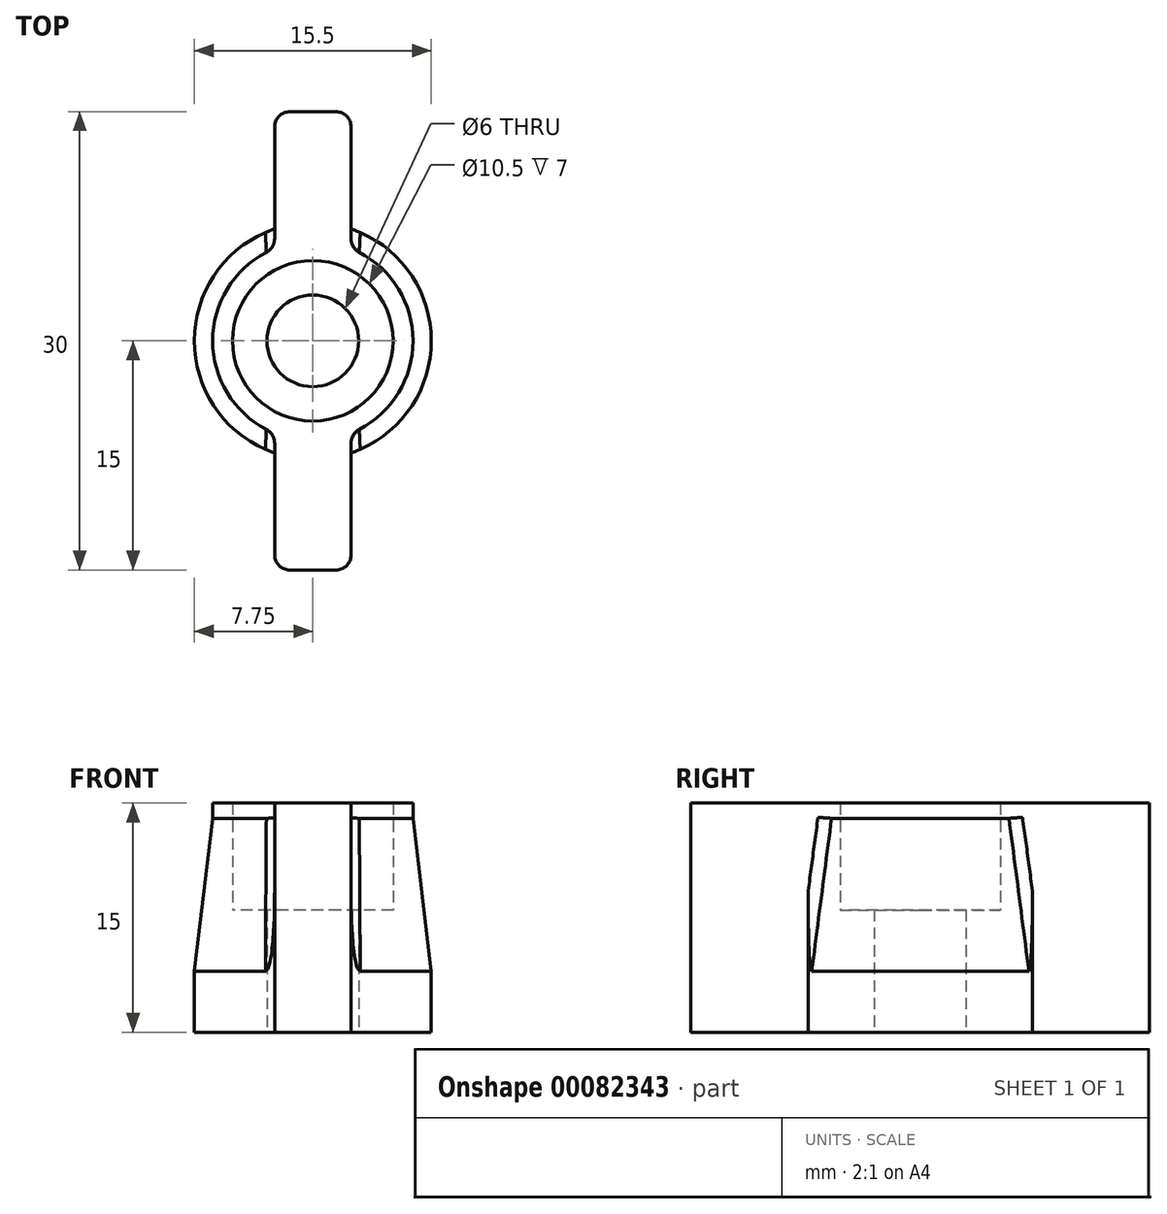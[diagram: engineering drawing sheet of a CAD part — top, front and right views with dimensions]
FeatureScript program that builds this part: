
annotation { "Feature Type Name" : "Feature", "Feature Type Description" : "" }
export const myFeature = defineFeature(function(context is Context, id is Id, definition is map)
    precondition{}
    {
        {
            var Q0;
            Q0=qCreatedBy(makeId("Top.planeOp"),FACE);
            var sketch = newSketch(context, id + "F0", { "sketchPlane" : qUnion([Q0])});
            skCircle(sketch, "E0", {"center": v(0, 0) * mm, "radius": 7.75 * mm});
            skCircle(sketch, "E1", {"center": v(0, 0) * mm, "radius": 5.25 * mm});
            skCircle(sketch, "E2", {"center": v(0, 0) * mm, "radius": 3 * mm});
            skLineSegment(sketch, "E3", {"start": v(0, 15) * mm, "end": v(-2.5, 15) * mm});
            skLineSegment(sketch, "E4", {"start": v(-2.5, 15) * mm, "end": v(-2.5, 4.62) * mm});
            skLineSegment(sketch, "E5", {"start": v(-2.5, 4.62) * mm, "end": v(0, 4.62) * mm});
            skLineSegment(sketch, "E6.MirrorCS", {"start": v(0, 15) * mm, "end": v(2.5, 15) * mm});
            skLineSegment(sketch, "E7.MirrorCS", {"start": v(2.5, 15) * mm, "end": v(2.5, 4.62) * mm});
            skLineSegment(sketch, "E8.MirrorCS", {"start": v(2.5, 4.62) * mm, "end": v(0, 4.62) * mm});
            skLineSegment(sketch, "E9.MirrorCS", {"start": v(-2.5, -4.62) * mm, "end": v(0, -4.62) * mm});
            skLineSegment(sketch, "E10.MirrorCS", {"start": v(-2.5, -15) * mm, "end": v(-2.5, -4.62) * mm});
            skLineSegment(sketch, "E11.MirrorCS", {"start": v(0, -15) * mm, "end": v(-2.5, -15) * mm});
            skLineSegment(sketch, "E12.MirrorCS", {"start": v(0, -15) * mm, "end": v(2.5, -15) * mm});
            skLineSegment(sketch, "E13.MirrorCS", {"start": v(2.5, -15) * mm, "end": v(2.5, -4.62) * mm});
            skLineSegment(sketch, "E14.MirrorCS", {"start": v(2.5, -4.62) * mm, "end": v(0, -4.62) * mm});
            skSolve(sketch);
        }
        {
            var Q0;
            {var subQ0=sQuery(id+"F0.wireOp",EDGE,"E4");var subQ1=sQuery(id+"F0.wireOp",EDGE,"E0");var subQ2=makeQuery(id+"F0.imprint","INTERSECT",VERTEX,{"derivedFrom":[subQ1,subQ0]});Q0=makeQuery(id+"F0.imprint","IMPRINT",FACE,{"disambiguationData":[TD([[makeQuery(id+"F0.imprint","IMPRINT",EDGE,{"disambiguationData":[TD([[subQ2,-1.0]])],"derivedFrom":subQ1}),1.0]])]});}
            var Q1;
            {var subQ0=sQuery(id+"F0.wireOp",EDGE,"E4");var subQ1=sQuery(id+"F0.wireOp",EDGE,"E0");var subQ2=makeQuery(id+"F0.imprint","INTERSECT",VERTEX,{"derivedFrom":[subQ1,subQ0]});Q1=makeQuery(id+"F0.imprint","IMPRINT",FACE,{"disambiguationData":[TD([[makeQuery(id+"F0.imprint","IMPRINT",EDGE,{"disambiguationData":[TD([[subQ2,1.0]])],"derivedFrom":subQ1}),1.0]])]});}
            var Q2;
            {var subQ0=sQuery(id+"F0.wireOp",EDGE,"E7.MirrorCS");var subQ1=sQuery(id+"F0.wireOp",EDGE,"E0");var subQ2=makeQuery(id+"F0.imprint","INTERSECT",VERTEX,{"derivedFrom":[subQ1,subQ0]});Q2=makeQuery(id+"F0.imprint","IMPRINT",FACE,{"disambiguationData":[TD([[makeQuery(id+"F0.imprint","IMPRINT",EDGE,{"disambiguationData":[TD([[subQ2,1.0]])],"derivedFrom":subQ1}),1.0]])]});}
            var Q3;
            {var subQ0=sQuery(id+"F0.wireOp",EDGE,"E10.MirrorCS");var subQ1=sQuery(id+"F0.wireOp",EDGE,"E0");var subQ2=makeQuery(id+"F0.imprint","INTERSECT",VERTEX,{"derivedFrom":[subQ1,subQ0]});Q3=makeQuery(id+"F0.imprint","IMPRINT",FACE,{"disambiguationData":[TD([[makeQuery(id+"F0.imprint","IMPRINT",EDGE,{"disambiguationData":[TD([[subQ2,-1.0]])],"derivedFrom":subQ1}),1.0]])]});}
            extrude(context, id + "F1", {"entities" : qUnion([Q0, Q1, Q2, Q3]), "depth" : 2 * mm});
        }
        {
            var Q0;
            {var subQ0=sQuery(id+"F0.wireOp",EDGE,"E5");Q0=makeQuery(id+"F0.imprint","IMPRINT",FACE,{"disambiguationData":[TD([[makeQuery(id+"F0.imprint","IMPRINT",EDGE,{"derivedFrom":subQ0}),1.0]])]});}
            var Q1;
            Q1=makeQuery(id+"F0.imprint","IMPRINT",FACE,{"disambiguationData":[TD([[makeQuery(id+"F0.imprint","IMPRINT",EDGE,{"derivedFrom":sQuery(id+"F0.wireOp",EDGE,"E2")}),-1.0]])]});
            var Q2;
            {var subQ0=sQuery(id+"F0.wireOp",EDGE,"E9.MirrorCS");Q2=makeQuery(id+"F0.imprint","IMPRINT",FACE,{"disambiguationData":[TD([[makeQuery(id+"F0.imprint","IMPRINT",EDGE,{"derivedFrom":subQ0}),-1.0]])]});}
            extrude(context, id + "F2", {"entities" : qUnion([Q0, Q1, Q2]), "operationType" : NewBodyOperationType.ADD, "depth" : 8 * mm});
        }
        {
            var Q0;
            {var subQ2=sQuery(id+"F0.wireOp",EDGE,"E3");Q0=makeQuery(id+"F0.imprint","IMPRINT",FACE,{"disambiguationData":[TD([[makeQuery(id+"F0.imprint","IMPRINT",EDGE,{"derivedFrom":subQ2}),1.0]])]});}
            var Q1;
            {var subQ0=sQuery(id+"F0.wireOp",EDGE,"E4");var subQ1=sQuery(id+"F0.wireOp",EDGE,"E0");var subQ2=makeQuery(id+"F0.imprint","INTERSECT",VERTEX,{"derivedFrom":[subQ1,subQ0]});Q1=makeQuery(id+"F0.imprint","IMPRINT",FACE,{"disambiguationData":[TD([[makeQuery(id+"F0.imprint","IMPRINT",EDGE,{"disambiguationData":[TD([[subQ2,1.0]])],"derivedFrom":subQ1}),1.0]])]});}
            var Q2;
            {var subQ0=sQuery(id+"F0.wireOp",EDGE,"E10.MirrorCS");var subQ1=sQuery(id+"F0.wireOp",EDGE,"E0");var subQ2=makeQuery(id+"F0.imprint","INTERSECT",VERTEX,{"derivedFrom":[subQ1,subQ0]});Q2=makeQuery(id+"F0.imprint","IMPRINT",FACE,{"disambiguationData":[TD([[makeQuery(id+"F0.imprint","IMPRINT",EDGE,{"disambiguationData":[TD([[subQ2,-1.0]])],"derivedFrom":subQ1}),1.0]])]});}
            var Q3;
            {var subQ1=sQuery(id+"F0.wireOp",EDGE,"E11.MirrorCS");Q3=makeQuery(id+"F0.imprint","IMPRINT",FACE,{"disambiguationData":[TD([[makeQuery(id+"F0.imprint","IMPRINT",EDGE,{"derivedFrom":subQ1}),-1.0]])]});}
            extrude(context, id + "F3", {"entities" : qUnion([Q0, Q1, Q2, Q3]), "operationType" : NewBodyOperationType.ADD, "depth" : 14 * mm});
        }
        {
            var Q0;
            {var subQ0=sQuery(id+"F0.wireOp",EDGE,"E0");var subQ1=sQuery(id+"F0.wireOp",EDGE,"E1");Q0=makeQuery(id+"F3.boolean.opBoolean","SPLIT",FACE,{"disambiguationData":[TD([makeQuery(id+"F3.opExtrude","SWEPT_FACE",FACE,{"disambiguationData":[OSD([sQuery(id+"F0.wireOp",EDGE,"E4")])]})])],"derivedFrom":makeQuery(id+"F1.opExtrude","CAP_FACE",FACE,{"disambiguationData":[OSD([subQ0,subQ1])],"isStart":false})});}
            var Q1;
            {var subQ0=sQuery(id+"F0.wireOp",EDGE,"E0");var subQ1=sQuery(id+"F0.wireOp",EDGE,"E1");Q1=makeQuery(id+"F3.boolean.opBoolean","SPLIT",FACE,{"disambiguationData":[TD([makeQuery(id+"F3.opExtrude","SWEPT_FACE",FACE,{"disambiguationData":[OSD([sQuery(id+"F0.wireOp",EDGE,"E7.MirrorCS")])]})])],"derivedFrom":makeQuery(id+"F1.opExtrude","CAP_FACE",FACE,{"disambiguationData":[OSD([subQ0,subQ1])],"isStart":false})});}
            extrude(context, id + "F4", {"entities" : qUnion([Q0, Q1]), "operationType" : NewBodyOperationType.ADD, "depth" : 12 * mm});
        }
        {
            var Q0;
            {var subQ0=sQuery(id+"F0.wireOp",EDGE,"E0");Q0=makeQuery(id+"F4.opExtrude","CAP_EDGE",EDGE,{"disambiguationData":[OSD([subQ0]),TDD([makeQuery(id+"F3.boolean.opBoolean","SPLIT",EDGE,{"disambiguationData":[TD([makeQuery(id+"F3.opExtrude","SWEPT_FACE",FACE,{"disambiguationData":[OSD([sQuery(id+"F0.wireOp",EDGE,"E7.MirrorCS")])]})])],"derivedFrom":makeQuery(id+"F1.opExtrude","CAP_EDGE",EDGE,{"disambiguationData":[OSD([subQ0])],"isStart":false})})])],"isStart":false});}
            var Q1;
            {var subQ0=sQuery(id+"F0.wireOp",EDGE,"E0");Q1=makeQuery(id+"F4.opExtrude","CAP_EDGE",EDGE,{"disambiguationData":[OSD([subQ0]),TDD([makeQuery(id+"F3.boolean.opBoolean","SPLIT",EDGE,{"disambiguationData":[TD([makeQuery(id+"F3.opExtrude","SWEPT_FACE",FACE,{"disambiguationData":[OSD([sQuery(id+"F0.wireOp",EDGE,"E4")])]})])],"derivedFrom":makeQuery(id+"F1.opExtrude","CAP_EDGE",EDGE,{"disambiguationData":[OSD([subQ0])],"isStart":false})})])],"isStart":false});}
            chamfer(context, id + "F5", {"entities" : qUnion([Q0, Q1]), "chamferType" : ChamferType.TWO_OFFSETS, "width1" : 1.2 * mm, "oppositeDirection" : false, "width2" : 10 * mm, "tangentPropagation" : true});
        }
        {
            var Q0;
            {var subQ0=sQuery(id+"F0.wireOp",EDGE,"E0");var subQ2=sQuery(id+"F0.wireOp",EDGE,"E7.MirrorCS");var subQ3=sQuery(id+"F0.wireOp",EDGE,"E13.MirrorCS");var subQ4=sQuery(id+"F0.wireOp",EDGE,"E1");var subQ6=makeQuery(id+"F1.opExtrude","CAP_FACE",FACE,{"disambiguationData":[OSD([subQ0,subQ4])],"isStart":false});var subQ7=sQuery(id+"F0.wireOp",EDGE,"E10.MirrorCS");var subQ8=sQuery(id+"F0.wireOp",EDGE,"E4");Q0=makeQuery(id+"F4.boolean.opBoolean","MERGE",FACE,{"derivedFrom":[makeQuery(id+"F3.opExtrude","CAP_FACE",FACE,{"disambiguationData":[OSD([subQ4,sQuery(id+"F0.wireOp",EDGE,"E3"),subQ8,sQuery(id+"F0.wireOp",EDGE,"E6.MirrorCS"),subQ2])],"isStart":false}),makeQuery(id+"F3.opExtrude","CAP_FACE",FACE,{"disambiguationData":[OSD([subQ4,subQ7,sQuery(id+"F0.wireOp",EDGE,"E11.MirrorCS"),sQuery(id+"F0.wireOp",EDGE,"E12.MirrorCS"),subQ3])],"isStart":false}),makeQuery(id+"F4.opExtrude","CAP_FACE",FACE,{"disambiguationData":[OSD([subQ0,subQ4]),TDD([makeQuery(id+"F3.boolean.opBoolean","SPLIT",FACE,{"disambiguationData":[TD([makeQuery(id+"F3.opExtrude","SWEPT_FACE",FACE,{"disambiguationData":[OSD([subQ8])]})])],"derivedFrom":subQ6})])],"isStart":false}),makeQuery(id+"F4.opExtrude","CAP_FACE",FACE,{"disambiguationData":[OSD([subQ0,subQ4]),TDD([makeQuery(id+"F3.boolean.opBoolean","SPLIT",FACE,{"disambiguationData":[TD([makeQuery(id+"F3.opExtrude","SWEPT_FACE",FACE,{"disambiguationData":[OSD([subQ2])]})])],"derivedFrom":subQ6})])],"isStart":false})]});}
            extrude(context, id + "F6", {"entities" : qUnion([Q0]), "operationType" : NewBodyOperationType.ADD, "depth" : 1 * mm});
        }
        {
            var Q0;
            {var subQ0=sQuery(id+"F0.wireOp",EDGE,"E13.MirrorCS");var subQ1=sQuery(id+"F0.wireOp",EDGE,"E12.MirrorCS");Q0=makeQuery(id+"F6.boolean.opBoolean","MERGE",EDGE,{"derivedFrom":[makeQuery(id+"F3.opExtrude","SWEPT_EDGE",EDGE,{"disambiguationData":[OSD([subQ1,subQ0])]}),makeQuery(id+"F6.opExtrude","SWEPT_EDGE",EDGE,{"disambiguationData":[OSD([subQ1,subQ0])]})]});}
            var Q1;
            {var subQ0=sQuery(id+"F0.wireOp",EDGE,"E11.MirrorCS");var subQ1=sQuery(id+"F0.wireOp",EDGE,"E10.MirrorCS");Q1=makeQuery(id+"F6.boolean.opBoolean","MERGE",EDGE,{"derivedFrom":[makeQuery(id+"F3.opExtrude","SWEPT_EDGE",EDGE,{"disambiguationData":[OSD([subQ1,subQ0])]}),makeQuery(id+"F6.opExtrude","SWEPT_EDGE",EDGE,{"disambiguationData":[OSD([subQ1,subQ0])]})]});}
            var Q2;
            {var subQ0=sQuery(id+"F0.wireOp",EDGE,"E7.MirrorCS");var subQ1=sQuery(id+"F0.wireOp",EDGE,"E6.MirrorCS");Q2=makeQuery(id+"F6.boolean.opBoolean","MERGE",EDGE,{"derivedFrom":[makeQuery(id+"F3.opExtrude","SWEPT_EDGE",EDGE,{"disambiguationData":[OSD([subQ1,subQ0])]}),makeQuery(id+"F6.opExtrude","SWEPT_EDGE",EDGE,{"disambiguationData":[OSD([subQ1,subQ0])]})]});}
            var Q3;
            {var subQ0=sQuery(id+"F0.wireOp",EDGE,"E4");var subQ1=sQuery(id+"F0.wireOp",EDGE,"E3");Q3=makeQuery(id+"F6.boolean.opBoolean","MERGE",EDGE,{"derivedFrom":[makeQuery(id+"F3.opExtrude","SWEPT_EDGE",EDGE,{"disambiguationData":[OSD([subQ1,subQ0])]}),makeQuery(id+"F6.opExtrude","SWEPT_EDGE",EDGE,{"disambiguationData":[OSD([subQ1,subQ0])]})]});}
            var Q4;
            {var subQ0=makeQuery(id+"F3.opExtrude","SWEPT_FACE",FACE,{"disambiguationData":[OSD([sQuery(id+"F0.wireOp",EDGE,"E7.MirrorCS")])]});var subQ1=sQuery(id+"F0.wireOp",EDGE,"E0");Q4=makeQuery(id+"F5.opChamfer","BLEND_EDGE",EDGE,{"blendedFrom":[makeQuery(id+"F4.opExtrude","CAP_EDGE",EDGE,{"disambiguationData":[OSD([subQ1]),TDD([makeQuery(id+"F3.boolean.opBoolean","SPLIT",EDGE,{"disambiguationData":[TD([subQ0])],"derivedFrom":makeQuery(id+"F1.opExtrude","CAP_EDGE",EDGE,{"disambiguationData":[OSD([subQ1])],"isStart":false})})])],"isStart":false}),subQ0],"blendedInto":[subQ0]});}
            var Q5;
            {var subQ0=sQuery(id+"F0.wireOp",EDGE,"E7.MirrorCS");var subQ1=makeQuery(id+"F3.opExtrude","SWEPT_FACE",FACE,{"disambiguationData":[OSD([subQ0])]});var subQ2=sQuery(id+"F0.wireOp",EDGE,"E1");var subQ3=sQuery(id+"F0.wireOp",EDGE,"E0");var subQ4=makeQuery(id+"F1.opExtrude","SWEPT_FACE",FACE,{"disambiguationData":[OSD([subQ3])]});Q5=makeQuery(id+"F4.boolean.opBoolean","MERGE",EDGE,{"derivedFrom":[makeQuery(id+"F3.boolean.opBoolean","INTERSECT",EDGE,{"derivedFrom":[subQ4,subQ1]}),makeQuery(id+"F4.opExtrude","SWEPT_EDGE",EDGE,{"disambiguationData":[OSD([subQ3,subQ2,subQ0]),TDD([makeQuery(id+"F3.boolean.opBoolean","INTERSECT",VERTEX,{"derivedFrom":[subQ4,makeQuery(id+"F1.opExtrude","CAP_FACE",FACE,{"disambiguationData":[OSD([subQ3,subQ2])],"isStart":false}),subQ1]})])]})]});}
            var Q6;
            {var subQ0=makeQuery(id+"F3.opExtrude","SWEPT_FACE",FACE,{"disambiguationData":[OSD([sQuery(id+"F0.wireOp",EDGE,"E13.MirrorCS")])]});var subQ1=sQuery(id+"F0.wireOp",EDGE,"E0");Q6=makeQuery(id+"F5.opChamfer","BLEND_EDGE",EDGE,{"blendedFrom":[makeQuery(id+"F4.opExtrude","CAP_EDGE",EDGE,{"disambiguationData":[OSD([subQ1]),TDD([makeQuery(id+"F3.boolean.opBoolean","SPLIT",EDGE,{"disambiguationData":[TD([makeQuery(id+"F3.opExtrude","SWEPT_FACE",FACE,{"disambiguationData":[OSD([sQuery(id+"F0.wireOp",EDGE,"E7.MirrorCS")])]})])],"derivedFrom":makeQuery(id+"F1.opExtrude","CAP_EDGE",EDGE,{"disambiguationData":[OSD([subQ1])],"isStart":false})})])],"isStart":false}),subQ0],"blendedInto":[subQ0]});}
            var Q7;
            {var subQ0=sQuery(id+"F0.wireOp",EDGE,"E13.MirrorCS");var subQ1=makeQuery(id+"F3.opExtrude","SWEPT_FACE",FACE,{"disambiguationData":[OSD([subQ0])]});var subQ2=sQuery(id+"F0.wireOp",EDGE,"E1");var subQ3=sQuery(id+"F0.wireOp",EDGE,"E0");var subQ4=makeQuery(id+"F1.opExtrude","SWEPT_FACE",FACE,{"disambiguationData":[OSD([subQ3])]});Q7=makeQuery(id+"F4.boolean.opBoolean","MERGE",EDGE,{"derivedFrom":[makeQuery(id+"F3.boolean.opBoolean","INTERSECT",EDGE,{"derivedFrom":[subQ4,subQ1]}),makeQuery(id+"F4.opExtrude","SWEPT_EDGE",EDGE,{"disambiguationData":[OSD([subQ3,subQ2,subQ0]),TDD([makeQuery(id+"F3.boolean.opBoolean","INTERSECT",VERTEX,{"derivedFrom":[subQ4,makeQuery(id+"F1.opExtrude","CAP_FACE",FACE,{"disambiguationData":[OSD([subQ3,subQ2])],"isStart":false}),subQ1]})])]})]});}
            var Q8;
            {var subQ0=makeQuery(id+"F3.opExtrude","SWEPT_FACE",FACE,{"disambiguationData":[OSD([sQuery(id+"F0.wireOp",EDGE,"E10.MirrorCS")])]});var subQ1=sQuery(id+"F0.wireOp",EDGE,"E0");Q8=makeQuery(id+"F5.opChamfer","BLEND_EDGE",EDGE,{"blendedFrom":[makeQuery(id+"F4.opExtrude","CAP_EDGE",EDGE,{"disambiguationData":[OSD([subQ1]),TDD([makeQuery(id+"F3.boolean.opBoolean","SPLIT",EDGE,{"disambiguationData":[TD([makeQuery(id+"F3.opExtrude","SWEPT_FACE",FACE,{"disambiguationData":[OSD([sQuery(id+"F0.wireOp",EDGE,"E4")])]})])],"derivedFrom":makeQuery(id+"F1.opExtrude","CAP_EDGE",EDGE,{"disambiguationData":[OSD([subQ1])],"isStart":false})})])],"isStart":false}),subQ0],"blendedInto":[subQ0]});}
            var Q9;
            {var subQ0=sQuery(id+"F0.wireOp",EDGE,"E10.MirrorCS");var subQ1=makeQuery(id+"F3.opExtrude","SWEPT_FACE",FACE,{"disambiguationData":[OSD([subQ0])]});var subQ2=sQuery(id+"F0.wireOp",EDGE,"E1");var subQ3=sQuery(id+"F0.wireOp",EDGE,"E0");var subQ4=makeQuery(id+"F1.opExtrude","SWEPT_FACE",FACE,{"disambiguationData":[OSD([subQ3])]});Q9=makeQuery(id+"F4.boolean.opBoolean","MERGE",EDGE,{"derivedFrom":[makeQuery(id+"F3.boolean.opBoolean","INTERSECT",EDGE,{"derivedFrom":[subQ4,subQ1]}),makeQuery(id+"F4.opExtrude","SWEPT_EDGE",EDGE,{"disambiguationData":[OSD([subQ3,subQ2,subQ0]),TDD([makeQuery(id+"F3.boolean.opBoolean","INTERSECT",VERTEX,{"derivedFrom":[subQ4,makeQuery(id+"F1.opExtrude","CAP_FACE",FACE,{"disambiguationData":[OSD([subQ3,subQ2])],"isStart":false}),subQ1]})])]})]});}
            var Q10;
            {var subQ0=makeQuery(id+"F3.opExtrude","SWEPT_FACE",FACE,{"disambiguationData":[OSD([sQuery(id+"F0.wireOp",EDGE,"E4")])]});var subQ1=sQuery(id+"F0.wireOp",EDGE,"E0");Q10=makeQuery(id+"F5.opChamfer","BLEND_EDGE",EDGE,{"blendedFrom":[makeQuery(id+"F4.opExtrude","CAP_EDGE",EDGE,{"disambiguationData":[OSD([subQ1]),TDD([makeQuery(id+"F3.boolean.opBoolean","SPLIT",EDGE,{"disambiguationData":[TD([subQ0])],"derivedFrom":makeQuery(id+"F1.opExtrude","CAP_EDGE",EDGE,{"disambiguationData":[OSD([subQ1])],"isStart":false})})])],"isStart":false}),subQ0],"blendedInto":[subQ0]});}
            var Q11;
            {var subQ0=sQuery(id+"F0.wireOp",EDGE,"E4");var subQ1=makeQuery(id+"F3.opExtrude","SWEPT_FACE",FACE,{"disambiguationData":[OSD([subQ0])]});var subQ2=sQuery(id+"F0.wireOp",EDGE,"E1");var subQ3=sQuery(id+"F0.wireOp",EDGE,"E0");var subQ4=makeQuery(id+"F1.opExtrude","SWEPT_FACE",FACE,{"disambiguationData":[OSD([subQ3])]});Q11=makeQuery(id+"F4.boolean.opBoolean","MERGE",EDGE,{"derivedFrom":[makeQuery(id+"F3.boolean.opBoolean","INTERSECT",EDGE,{"derivedFrom":[subQ4,subQ1]}),makeQuery(id+"F4.opExtrude","SWEPT_EDGE",EDGE,{"disambiguationData":[OSD([subQ3,subQ2,subQ0]),TDD([makeQuery(id+"F3.boolean.opBoolean","INTERSECT",VERTEX,{"derivedFrom":[subQ4,makeQuery(id+"F1.opExtrude","CAP_FACE",FACE,{"disambiguationData":[OSD([subQ3,subQ2])],"isStart":false}),subQ1]})])]})]});}
            var Q12;
            {var subQ0=sQuery(id+"F0.wireOp",EDGE,"E4");var subQ1=makeQuery(id+"F3.opExtrude","SWEPT_FACE",FACE,{"disambiguationData":[OSD([subQ0])]});var subQ2=sQuery(id+"F0.wireOp",EDGE,"E0");var subQ4=sQuery(id+"F0.wireOp",EDGE,"E7.MirrorCS");var subQ5=sQuery(id+"F0.wireOp",EDGE,"E13.MirrorCS");var subQ6=sQuery(id+"F0.wireOp",EDGE,"E1");var subQ8=makeQuery(id+"F1.opExtrude","CAP_FACE",FACE,{"disambiguationData":[OSD([subQ2,subQ6])],"isStart":false});var subQ9=sQuery(id+"F0.wireOp",EDGE,"E10.MirrorCS");var subQ11=sQuery(id+"F0.wireOp",EDGE,"E12.MirrorCS");var subQ12=sQuery(id+"F0.wireOp",EDGE,"E11.MirrorCS");var subQ13=sQuery(id+"F0.wireOp",EDGE,"E6.MirrorCS");var subQ14=sQuery(id+"F0.wireOp",EDGE,"E3");Q12=makeQuery(id+"F6.opExtrude","SWEPT_EDGE",EDGE,{"disambiguationData":[OSD([subQ2,subQ6,subQ14,subQ0,subQ13,subQ4,subQ9,subQ12,subQ11,subQ5]),TDD([makeQuery(id+"F5.opChamfer","BLEND_VERTEX",VERTEX,{"blendedFrom":[makeQuery(id+"F4.opExtrude","CAP_EDGE",EDGE,{"disambiguationData":[OSD([subQ2]),TDD([makeQuery(id+"F3.boolean.opBoolean","SPLIT",EDGE,{"disambiguationData":[TD([subQ1])],"derivedFrom":makeQuery(id+"F1.opExtrude","CAP_EDGE",EDGE,{"disambiguationData":[OSD([subQ2])],"isStart":false})})])],"isStart":false}),makeQuery(id+"F4.boolean.opBoolean","MERGE",FACE,{"derivedFrom":[makeQuery(id+"F3.opExtrude","CAP_FACE",FACE,{"disambiguationData":[OSD([subQ6,subQ14,subQ0,subQ13,subQ4])],"isStart":false}),makeQuery(id+"F3.opExtrude","CAP_FACE",FACE,{"disambiguationData":[OSD([subQ6,subQ9,subQ12,subQ11,subQ5])],"isStart":false}),makeQuery(id+"F4.opExtrude","CAP_FACE",FACE,{"disambiguationData":[OSD([subQ2,subQ6]),TDD([makeQuery(id+"F3.boolean.opBoolean","SPLIT",FACE,{"disambiguationData":[TD([subQ1])],"derivedFrom":subQ8})])],"isStart":false}),makeQuery(id+"F4.opExtrude","CAP_FACE",FACE,{"disambiguationData":[OSD([subQ2,subQ6]),TDD([makeQuery(id+"F3.boolean.opBoolean","SPLIT",FACE,{"disambiguationData":[TD([makeQuery(id+"F3.opExtrude","SWEPT_FACE",FACE,{"disambiguationData":[OSD([subQ4])]})])],"derivedFrom":subQ8})])],"isStart":false})]}),subQ1],"blendedInto":[makeQuery(id+"F4.boolean.opBoolean","MERGE",FACE,{"derivedFrom":[makeQuery(id+"F3.opExtrude","CAP_FACE",FACE,{"disambiguationData":[OSD([subQ6,subQ14,subQ0,subQ13,subQ4])],"isStart":false}),makeQuery(id+"F3.opExtrude","CAP_FACE",FACE,{"disambiguationData":[OSD([subQ6,subQ9,subQ12,subQ11,subQ5])],"isStart":false}),makeQuery(id+"F4.opExtrude","CAP_FACE",FACE,{"disambiguationData":[OSD([subQ2,subQ6]),TDD([makeQuery(id+"F3.boolean.opBoolean","SPLIT",FACE,{"disambiguationData":[TD([subQ1])],"derivedFrom":subQ8})])],"isStart":false}),makeQuery(id+"F4.opExtrude","CAP_FACE",FACE,{"disambiguationData":[OSD([subQ2,subQ6]),TDD([makeQuery(id+"F3.boolean.opBoolean","SPLIT",FACE,{"disambiguationData":[TD([makeQuery(id+"F3.opExtrude","SWEPT_FACE",FACE,{"disambiguationData":[OSD([subQ4])]})])],"derivedFrom":subQ8})])],"isStart":false})]}),subQ1]})])]});}
            var Q13;
            {var subQ0=sQuery(id+"F0.wireOp",EDGE,"E10.MirrorCS");var subQ1=makeQuery(id+"F3.opExtrude","SWEPT_FACE",FACE,{"disambiguationData":[OSD([subQ0])]});var subQ2=sQuery(id+"F0.wireOp",EDGE,"E0");var subQ4=sQuery(id+"F0.wireOp",EDGE,"E7.MirrorCS");var subQ5=sQuery(id+"F0.wireOp",EDGE,"E13.MirrorCS");var subQ6=sQuery(id+"F0.wireOp",EDGE,"E1");var subQ8=makeQuery(id+"F1.opExtrude","CAP_FACE",FACE,{"disambiguationData":[OSD([subQ2,subQ6])],"isStart":false});var subQ9=sQuery(id+"F0.wireOp",EDGE,"E4");var subQ10=makeQuery(id+"F3.opExtrude","SWEPT_FACE",FACE,{"disambiguationData":[OSD([subQ9])]});var subQ11=sQuery(id+"F0.wireOp",EDGE,"E12.MirrorCS");var subQ12=sQuery(id+"F0.wireOp",EDGE,"E11.MirrorCS");var subQ13=sQuery(id+"F0.wireOp",EDGE,"E6.MirrorCS");var subQ14=sQuery(id+"F0.wireOp",EDGE,"E3");Q13=makeQuery(id+"F6.opExtrude","SWEPT_EDGE",EDGE,{"disambiguationData":[OSD([subQ2,subQ6,subQ14,subQ9,subQ13,subQ4,subQ0,subQ12,subQ11,subQ5]),TDD([makeQuery(id+"F5.opChamfer","BLEND_VERTEX",VERTEX,{"blendedFrom":[makeQuery(id+"F4.opExtrude","CAP_EDGE",EDGE,{"disambiguationData":[OSD([subQ2]),TDD([makeQuery(id+"F3.boolean.opBoolean","SPLIT",EDGE,{"disambiguationData":[TD([subQ10])],"derivedFrom":makeQuery(id+"F1.opExtrude","CAP_EDGE",EDGE,{"disambiguationData":[OSD([subQ2])],"isStart":false})})])],"isStart":false}),makeQuery(id+"F4.boolean.opBoolean","MERGE",FACE,{"derivedFrom":[makeQuery(id+"F3.opExtrude","CAP_FACE",FACE,{"disambiguationData":[OSD([subQ6,subQ14,subQ9,subQ13,subQ4])],"isStart":false}),makeQuery(id+"F3.opExtrude","CAP_FACE",FACE,{"disambiguationData":[OSD([subQ6,subQ0,subQ12,subQ11,subQ5])],"isStart":false}),makeQuery(id+"F4.opExtrude","CAP_FACE",FACE,{"disambiguationData":[OSD([subQ2,subQ6]),TDD([makeQuery(id+"F3.boolean.opBoolean","SPLIT",FACE,{"disambiguationData":[TD([subQ10])],"derivedFrom":subQ8})])],"isStart":false}),makeQuery(id+"F4.opExtrude","CAP_FACE",FACE,{"disambiguationData":[OSD([subQ2,subQ6]),TDD([makeQuery(id+"F3.boolean.opBoolean","SPLIT",FACE,{"disambiguationData":[TD([makeQuery(id+"F3.opExtrude","SWEPT_FACE",FACE,{"disambiguationData":[OSD([subQ4])]})])],"derivedFrom":subQ8})])],"isStart":false})]}),subQ1],"blendedInto":[makeQuery(id+"F4.boolean.opBoolean","MERGE",FACE,{"derivedFrom":[makeQuery(id+"F3.opExtrude","CAP_FACE",FACE,{"disambiguationData":[OSD([subQ6,subQ14,subQ9,subQ13,subQ4])],"isStart":false}),makeQuery(id+"F3.opExtrude","CAP_FACE",FACE,{"disambiguationData":[OSD([subQ6,subQ0,subQ12,subQ11,subQ5])],"isStart":false}),makeQuery(id+"F4.opExtrude","CAP_FACE",FACE,{"disambiguationData":[OSD([subQ2,subQ6]),TDD([makeQuery(id+"F3.boolean.opBoolean","SPLIT",FACE,{"disambiguationData":[TD([subQ10])],"derivedFrom":subQ8})])],"isStart":false}),makeQuery(id+"F4.opExtrude","CAP_FACE",FACE,{"disambiguationData":[OSD([subQ2,subQ6]),TDD([makeQuery(id+"F3.boolean.opBoolean","SPLIT",FACE,{"disambiguationData":[TD([makeQuery(id+"F3.opExtrude","SWEPT_FACE",FACE,{"disambiguationData":[OSD([subQ4])]})])],"derivedFrom":subQ8})])],"isStart":false})]}),subQ1]})])]});}
            var Q14;
            {var subQ0=sQuery(id+"F0.wireOp",EDGE,"E13.MirrorCS");var subQ1=makeQuery(id+"F3.opExtrude","SWEPT_FACE",FACE,{"disambiguationData":[OSD([subQ0])]});var subQ2=sQuery(id+"F0.wireOp",EDGE,"E0");var subQ4=sQuery(id+"F0.wireOp",EDGE,"E7.MirrorCS");var subQ5=makeQuery(id+"F3.opExtrude","SWEPT_FACE",FACE,{"disambiguationData":[OSD([subQ4])]});var subQ6=sQuery(id+"F0.wireOp",EDGE,"E1");var subQ8=makeQuery(id+"F1.opExtrude","CAP_FACE",FACE,{"disambiguationData":[OSD([subQ2,subQ6])],"isStart":false});var subQ9=sQuery(id+"F0.wireOp",EDGE,"E10.MirrorCS");var subQ10=sQuery(id+"F0.wireOp",EDGE,"E4");var subQ11=sQuery(id+"F0.wireOp",EDGE,"E12.MirrorCS");var subQ12=sQuery(id+"F0.wireOp",EDGE,"E11.MirrorCS");var subQ13=sQuery(id+"F0.wireOp",EDGE,"E6.MirrorCS");var subQ14=sQuery(id+"F0.wireOp",EDGE,"E3");Q14=makeQuery(id+"F6.opExtrude","SWEPT_EDGE",EDGE,{"disambiguationData":[OSD([subQ2,subQ6,subQ14,subQ10,subQ13,subQ4,subQ9,subQ12,subQ11,subQ0]),TDD([makeQuery(id+"F5.opChamfer","BLEND_VERTEX",VERTEX,{"blendedFrom":[makeQuery(id+"F4.opExtrude","CAP_EDGE",EDGE,{"disambiguationData":[OSD([subQ2]),TDD([makeQuery(id+"F3.boolean.opBoolean","SPLIT",EDGE,{"disambiguationData":[TD([subQ5])],"derivedFrom":makeQuery(id+"F1.opExtrude","CAP_EDGE",EDGE,{"disambiguationData":[OSD([subQ2])],"isStart":false})})])],"isStart":false}),makeQuery(id+"F4.boolean.opBoolean","MERGE",FACE,{"derivedFrom":[makeQuery(id+"F3.opExtrude","CAP_FACE",FACE,{"disambiguationData":[OSD([subQ6,subQ14,subQ10,subQ13,subQ4])],"isStart":false}),makeQuery(id+"F3.opExtrude","CAP_FACE",FACE,{"disambiguationData":[OSD([subQ6,subQ9,subQ12,subQ11,subQ0])],"isStart":false}),makeQuery(id+"F4.opExtrude","CAP_FACE",FACE,{"disambiguationData":[OSD([subQ2,subQ6]),TDD([makeQuery(id+"F3.boolean.opBoolean","SPLIT",FACE,{"disambiguationData":[TD([makeQuery(id+"F3.opExtrude","SWEPT_FACE",FACE,{"disambiguationData":[OSD([subQ10])]})])],"derivedFrom":subQ8})])],"isStart":false}),makeQuery(id+"F4.opExtrude","CAP_FACE",FACE,{"disambiguationData":[OSD([subQ2,subQ6]),TDD([makeQuery(id+"F3.boolean.opBoolean","SPLIT",FACE,{"disambiguationData":[TD([subQ5])],"derivedFrom":subQ8})])],"isStart":false})]}),subQ1],"blendedInto":[makeQuery(id+"F4.boolean.opBoolean","MERGE",FACE,{"derivedFrom":[makeQuery(id+"F3.opExtrude","CAP_FACE",FACE,{"disambiguationData":[OSD([subQ6,subQ14,subQ10,subQ13,subQ4])],"isStart":false}),makeQuery(id+"F3.opExtrude","CAP_FACE",FACE,{"disambiguationData":[OSD([subQ6,subQ9,subQ12,subQ11,subQ0])],"isStart":false}),makeQuery(id+"F4.opExtrude","CAP_FACE",FACE,{"disambiguationData":[OSD([subQ2,subQ6]),TDD([makeQuery(id+"F3.boolean.opBoolean","SPLIT",FACE,{"disambiguationData":[TD([makeQuery(id+"F3.opExtrude","SWEPT_FACE",FACE,{"disambiguationData":[OSD([subQ10])]})])],"derivedFrom":subQ8})])],"isStart":false}),makeQuery(id+"F4.opExtrude","CAP_FACE",FACE,{"disambiguationData":[OSD([subQ2,subQ6]),TDD([makeQuery(id+"F3.boolean.opBoolean","SPLIT",FACE,{"disambiguationData":[TD([subQ5])],"derivedFrom":subQ8})])],"isStart":false})]}),subQ1]})])]});}
            var Q15;
            {var subQ0=sQuery(id+"F0.wireOp",EDGE,"E7.MirrorCS");var subQ1=makeQuery(id+"F3.opExtrude","SWEPT_FACE",FACE,{"disambiguationData":[OSD([subQ0])]});var subQ2=sQuery(id+"F0.wireOp",EDGE,"E0");var subQ4=sQuery(id+"F0.wireOp",EDGE,"E13.MirrorCS");var subQ6=sQuery(id+"F0.wireOp",EDGE,"E1");var subQ8=makeQuery(id+"F1.opExtrude","CAP_FACE",FACE,{"disambiguationData":[OSD([subQ2,subQ6])],"isStart":false});var subQ9=sQuery(id+"F0.wireOp",EDGE,"E10.MirrorCS");var subQ10=sQuery(id+"F0.wireOp",EDGE,"E4");var subQ11=sQuery(id+"F0.wireOp",EDGE,"E12.MirrorCS");var subQ12=sQuery(id+"F0.wireOp",EDGE,"E11.MirrorCS");var subQ13=sQuery(id+"F0.wireOp",EDGE,"E6.MirrorCS");var subQ14=sQuery(id+"F0.wireOp",EDGE,"E3");Q15=makeQuery(id+"F6.opExtrude","SWEPT_EDGE",EDGE,{"disambiguationData":[OSD([subQ2,subQ6,subQ14,subQ10,subQ13,subQ0,subQ9,subQ12,subQ11,subQ4]),TDD([makeQuery(id+"F5.opChamfer","BLEND_VERTEX",VERTEX,{"blendedFrom":[makeQuery(id+"F4.opExtrude","CAP_EDGE",EDGE,{"disambiguationData":[OSD([subQ2]),TDD([makeQuery(id+"F3.boolean.opBoolean","SPLIT",EDGE,{"disambiguationData":[TD([subQ1])],"derivedFrom":makeQuery(id+"F1.opExtrude","CAP_EDGE",EDGE,{"disambiguationData":[OSD([subQ2])],"isStart":false})})])],"isStart":false}),makeQuery(id+"F4.boolean.opBoolean","MERGE",FACE,{"derivedFrom":[makeQuery(id+"F3.opExtrude","CAP_FACE",FACE,{"disambiguationData":[OSD([subQ6,subQ14,subQ10,subQ13,subQ0])],"isStart":false}),makeQuery(id+"F3.opExtrude","CAP_FACE",FACE,{"disambiguationData":[OSD([subQ6,subQ9,subQ12,subQ11,subQ4])],"isStart":false}),makeQuery(id+"F4.opExtrude","CAP_FACE",FACE,{"disambiguationData":[OSD([subQ2,subQ6]),TDD([makeQuery(id+"F3.boolean.opBoolean","SPLIT",FACE,{"disambiguationData":[TD([makeQuery(id+"F3.opExtrude","SWEPT_FACE",FACE,{"disambiguationData":[OSD([subQ10])]})])],"derivedFrom":subQ8})])],"isStart":false}),makeQuery(id+"F4.opExtrude","CAP_FACE",FACE,{"disambiguationData":[OSD([subQ2,subQ6]),TDD([makeQuery(id+"F3.boolean.opBoolean","SPLIT",FACE,{"disambiguationData":[TD([subQ1])],"derivedFrom":subQ8})])],"isStart":false})]}),subQ1],"blendedInto":[makeQuery(id+"F4.boolean.opBoolean","MERGE",FACE,{"derivedFrom":[makeQuery(id+"F3.opExtrude","CAP_FACE",FACE,{"disambiguationData":[OSD([subQ6,subQ14,subQ10,subQ13,subQ0])],"isStart":false}),makeQuery(id+"F3.opExtrude","CAP_FACE",FACE,{"disambiguationData":[OSD([subQ6,subQ9,subQ12,subQ11,subQ4])],"isStart":false}),makeQuery(id+"F4.opExtrude","CAP_FACE",FACE,{"disambiguationData":[OSD([subQ2,subQ6]),TDD([makeQuery(id+"F3.boolean.opBoolean","SPLIT",FACE,{"disambiguationData":[TD([makeQuery(id+"F3.opExtrude","SWEPT_FACE",FACE,{"disambiguationData":[OSD([subQ10])]})])],"derivedFrom":subQ8})])],"isStart":false}),makeQuery(id+"F4.opExtrude","CAP_FACE",FACE,{"disambiguationData":[OSD([subQ2,subQ6]),TDD([makeQuery(id+"F3.boolean.opBoolean","SPLIT",FACE,{"disambiguationData":[TD([subQ1])],"derivedFrom":subQ8})])],"isStart":false})]}),subQ1]})])]});}
            fillet(context, id + "F7", {"entities" : qUnion([Q0, Q1, Q2, Q3, Q4, Q5, Q6, Q7, Q8, Q9, Q10, Q11, Q12, Q13, Q14, Q15]), "radius" : 1 * mm, "tangentPropagation" : true, "allowEdgeOverflow" : false});
        }
    });
